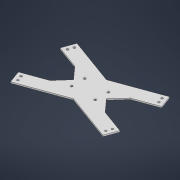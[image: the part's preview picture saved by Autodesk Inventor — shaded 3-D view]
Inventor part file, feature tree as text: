
AUTODESK INVENTOR PART (.ipt)
format: ipt  version: 2021 (Build 250183000, 183)  size: 293,888 bytes
history: native  units: mm
features: extrude x3, sketch x3, other x1
ambient origin geometry x8: Origin, YZ Plane, XZ Plane, XY Plane, X Axis, Y Axis, Z Axis, Center Point
bodies: Volumenkörper1 (feature_tree)
feature tree (7):
  other  "Kreuz_Halterung"
  extrude  "Extrusion1"  Depth=50.0mm
  extrude  "Extrusion2"  Depth=3.490659mm
  extrude  "Extrusion3"  TaperAngle=90.0deg  [1 undecoded]
  sketch  "Skizze1"  dims[d0=50.0mm d1=50.0mm]
  sketch  "Skizze2"  dims[d3=75.0mm d6=3.490659mm]
  sketch  "Skizze3"  dims[d7=20.0mm d8=90.0deg d12=7.306589mm d13=2.0mm d14=0.0mm d15=3.2mm d16=6.0mm d17=6.0mm d18=3.2mm d19=6.0mm d20=6.0mm d21=2.0mm d22=0.0mm d23=3.2mm d24=18.0mm d25=10.0mm d26=2.0mm d27=0.0mm]
note: 1 required parameter value undecoded (feature->parameter linkage not recoverable at this tier; creation-order binding heuristic only, values carry confidence <= 0.55)
